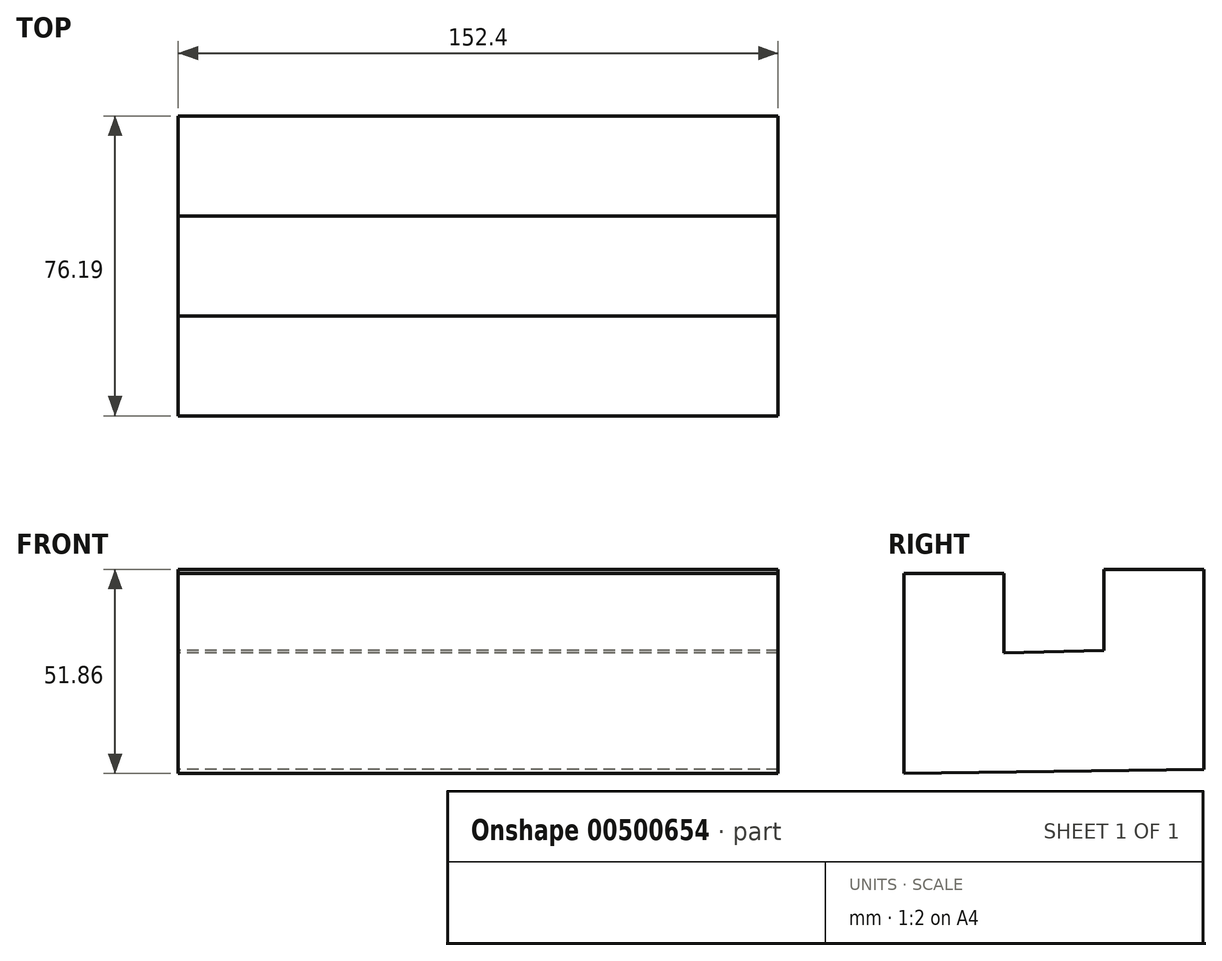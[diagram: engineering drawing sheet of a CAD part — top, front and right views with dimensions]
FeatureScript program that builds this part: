
annotation { "Feature Type Name" : "Feature", "Feature Type Description" : "" }
export const myFeature = defineFeature(function(context is Context, id is Id, definition is map)
    precondition{}
    {
        {
            var Q0;
            Q0=qCreatedBy(makeId("Right.planeOp"),FACE);
            var sketch = newSketch(context, id + "F0", { "sketchPlane" : qUnion([Q0])});
            skLineSegment(sketch, "E0", {"start": v(-50.51, 50.53) * mm, "end": v(-50.51, -0.27) * mm});
            skLineSegment(sketch, "E1", {"start": v(-50.51, 50.53) * mm, "end": v(-25.11, 50.53) * mm});
            skLineSegment(sketch, "E2", {"start": v(-25.11, 50.53) * mm, "end": v(-25.11, 30.35) * mm});
            skLineSegment(sketch, "E3", {"start": v(-25.11, 30.35) * mm, "end": v(0.28, 30.97) * mm});
            skLineSegment(sketch, "E4", {"start": v(0.28, 30.97) * mm, "end": v(0.28, 51.6) * mm});
            skLineSegment(sketch, "E5", {"start": v(0.28, 51.6) * mm, "end": v(25.68, 51.6) * mm});
            skLineSegment(sketch, "E6", {"start": v(25.68, 51.6) * mm, "end": v(25.68, 0.8) * mm});
            skLineSegment(sketch, "E7", {"start": v(-50.51, -0.27) * mm, "end": v(25.68, 0.8) * mm});
            skSolve(sketch);
        }
        {
            var Q0;
            Q0 = qSketchRegion(id + "F0", true);
            extrude(context, id + "F1", {"entities" : qUnion([Q0]), "depth" : 152.4 * mm});
        }
    });
